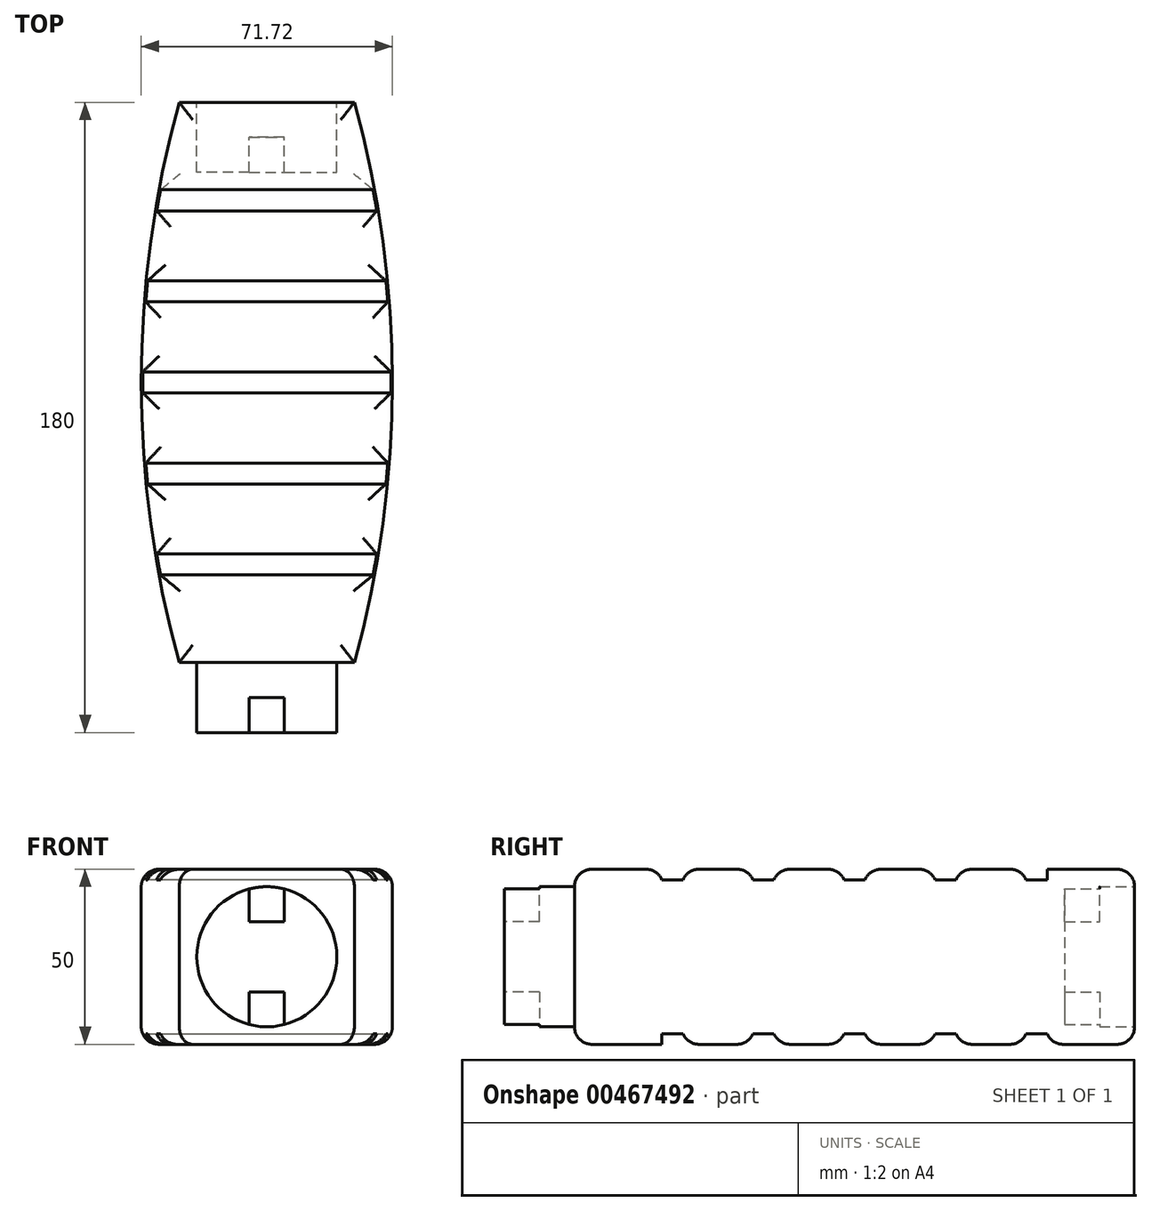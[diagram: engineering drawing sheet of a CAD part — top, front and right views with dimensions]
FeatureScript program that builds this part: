
annotation { "Feature Type Name" : "Feature", "Feature Type Description" : "" }
export const myFeature = defineFeature(function(context is Context, id is Id, definition is map)
    precondition{}
    {
        {
            var Q0;
            Q0=qCreatedBy(makeId("Top.planeOp"),FACE);
            var sketch = newSketch(context, id + "F0", { "sketchPlane" : qUnion([Q0])});
            skLineSegment(sketch, "E0.bottom", {"start": v(25, -80) * mm, "end": v(-25, -80) * mm});
            skLineSegment(sketch, "E0.top", {"start": v(25, 80) * mm, "end": v(-25, 80) * mm});
            skLineSegment(sketch, "E0.left", {"start": v(25, -80) * mm, "end": v(25, 80) * mm});
            skLineSegment(sketch, "E0.right", {"start": v(-25, -80) * mm, "end": v(-25, 80) * mm});
            skPoint(sketch, "E0.middle", {"position": v(0, 0) * mm});
            skArc(sketch, "E1", {"start": v(-25, 80) * mm, "mid": v(-35.86, 0) * mm, "end": v(-25, -80) * mm});
            skArc(sketch, "E2", {"start": v(25, -80) * mm, "mid": v(35.86, 0) * mm, "end": v(25, 80) * mm});
            skSolve(sketch);
        }
        {
            var Q0;
            Q0=makeQuery(id+"F0.imprint","IMPRINT",FACE,{"disambiguationData":[TD([[makeQuery(id+"F0.imprint","IMPRINT",EDGE,{"derivedFrom":sQuery(id+"F0.wireOp",EDGE,"E0.bottom")}),-1.0]])]});
            var Q1;
            Q1=makeQuery(id+"F0.imprint","IMPRINT",FACE,{"disambiguationData":[TD([[makeQuery(id+"F0.imprint","IMPRINT",EDGE,{"derivedFrom":sQuery(id+"F0.wireOp",EDGE,"E0.left")}),-1.0]])]});
            var Q2;
            Q2=makeQuery(id+"F0.imprint","IMPRINT",FACE,{"disambiguationData":[TD([[makeQuery(id+"F0.imprint","IMPRINT",EDGE,{"derivedFrom":sQuery(id+"F0.wireOp",EDGE,"E0.right")}),1.0]])]});
            extrude(context, id + "F1", {"entities" : qUnion([Q0, Q1, Q2]), "depth" : 50 * mm});
        }
        {
            var Q0;
            Q0=makeQuery(id+"F1.opExtrude","SWEPT_FACE",FACE,{"disambiguationData":[OSD([sQuery(id+"F0.wireOp",EDGE,"E0.bottom")])]});
            var sketch = newSketch(context, id + "F2", { "sketchPlane" : qUnion([Q0])});
            skCircle(sketch, "E3", {"center": v(0, 25) * mm, "radius": 20 * mm});
            skPoint(sketch, "E3.centerSnap0", {"position": v(25, 25) * mm});
            skSolve(sketch);
        }
        {
            var Q0;
            Q0=makeQuery(id+"F2.imprint","IMPRINT",FACE,{"disambiguationData":[TD([[makeQuery(id+"F2.imprint","IMPRINT",EDGE,{"derivedFrom":sQuery(id+"F2.wireOp",EDGE,"E3")}),1.0]])]});
            extrude(context, id + "F3", {"entities" : qUnion([Q0]), "operationType" : NewBodyOperationType.ADD, "depth" : 20 * mm});
        }
        {
            var Q0;
            Q0=makeQuery(id+"F3.opExtrude","CAP_FACE",FACE,{"disambiguationData":[OSD([sQuery(id+"F2.wireOp",EDGE,"E3")])],"isStart":false});
            var sketch = newSketch(context, id + "F4", { "sketchPlane" : qUnion([Q0])});
            skLineSegment(sketch, "E4", {"start": v(0, 45) * mm, "end": v(0, 35) * mm});
            skLineSegment(sketch, "E5", {"start": v(0, 35) * mm, "end": v(5, 35) * mm});
            skLineSegment(sketch, "E6", {"start": v(5, 35) * mm, "end": v(5, 44.36) * mm});
            skLineSegment(sketch, "E7", {"start": v(0, 35) * mm, "end": v(-5, 35) * mm});
            skLineSegment(sketch, "E8", {"start": v(-5, 35) * mm, "end": v(-5, 44.36) * mm});
            skLineSegment(sketch, "E9", {"start": v(0, 5) * mm, "end": v(0, 15) * mm});
            skLineSegment(sketch, "E10", {"start": v(0, 15) * mm, "end": v(5, 15) * mm});
            skLineSegment(sketch, "E11", {"start": v(5, 15) * mm, "end": v(5, 5.64) * mm});
            skLineSegment(sketch, "E12", {"start": v(0, 15) * mm, "end": v(-5, 15) * mm});
            skLineSegment(sketch, "E13", {"start": v(-5, 15) * mm, "end": v(-5, 5.64) * mm});
            skSolve(sketch);
        }
        {
            var Q0;
            Q0 = qSketchRegion(id + "F4", true);
            var Q1;
            {var subQ0=sQuery(id+"F4.wireOp",EDGE,"E4");Q1=makeQuery(id+"F4.imprint","IMPRINT",FACE,{"disambiguationData":[TD([[makeQuery(id+"F4.imprint","IMPRINT",EDGE,{"derivedFrom":subQ0}),1.0]])]});}
            var Q2;
            {var subQ0=sQuery(id+"F4.wireOp",EDGE,"E4");Q2=makeQuery(id+"F4.imprint","IMPRINT",FACE,{"disambiguationData":[TD([[makeQuery(id+"F4.imprint","IMPRINT",EDGE,{"derivedFrom":subQ0}),-1.0]])]});}
            var Q3;
            {var subQ0=sQuery(id+"F4.wireOp",EDGE,"E9");Q3=makeQuery(id+"F4.imprint","IMPRINT",FACE,{"disambiguationData":[TD([[makeQuery(id+"F4.imprint","IMPRINT",EDGE,{"derivedFrom":subQ0}),-1.0]])]});}
            var Q4;
            {var subQ0=sQuery(id+"F4.wireOp",EDGE,"E9");Q4=makeQuery(id+"F4.imprint","IMPRINT",FACE,{"disambiguationData":[TD([[makeQuery(id+"F4.imprint","IMPRINT",EDGE,{"derivedFrom":subQ0}),1.0]])]});}
            extrude(context, id + "F5", {"entities" : qUnion([Q0, Q1, Q2, Q3, Q4]), "operationType" : NewBodyOperationType.REMOVE, "oppositeDirection" : true, "depth" : 10 * mm});
        }
        {
            var Q0;
            Q0=makeQuery(id+"F1.opExtrude","CAP_FACE",FACE,{"disambiguationData":[OSD([sQuery(id+"F0.wireOp",EDGE,"E0.bottom"),sQuery(id+"F0.wireOp",EDGE,"E0.top"),sQuery(id+"F0.wireOp",EDGE,"E1"),sQuery(id+"F0.wireOp",EDGE,"E2")])],"isStart":false});
            var Q1;
            Q1=makeQuery(id+"F1.opExtrude","CAP_FACE",FACE,{"disambiguationData":[OSD([sQuery(id+"F0.wireOp",EDGE,"E0.bottom"),sQuery(id+"F0.wireOp",EDGE,"E0.top"),sQuery(id+"F0.wireOp",EDGE,"E1"),sQuery(id+"F0.wireOp",EDGE,"E2")])],"isStart":true});
            fillet(context, id + "F6", {"entities" : qUnion([Q0, Q1]), "radius" : 5 * mm, "tangentPropagation" : true, "allowEdgeOverflow" : false});
        }
        {
            var Q0;
            Q0=makeQuery(id+"F1.opExtrude","CAP_FACE",FACE,{"disambiguationData":[OSD([sQuery(id+"F0.wireOp",EDGE,"E0.bottom"),sQuery(id+"F0.wireOp",EDGE,"E0.top"),sQuery(id+"F0.wireOp",EDGE,"E1"),sQuery(id+"F0.wireOp",EDGE,"E2")])],"isStart":false});
            var sketch = newSketch(context, id + "F7", { "sketchPlane" : qUnion([Q0])});
            skLineSegment(sketch, "E14.bottom", {"start": v(57.86, 49) * mm, "end": v(-57.86, 49) * mm});
            skLineSegment(sketch, "E14.top", {"start": v(57.86, 55) * mm, "end": v(-57.86, 55) * mm});
            skLineSegment(sketch, "E14.left", {"start": v(57.86, 49) * mm, "end": v(57.86, 55) * mm});
            skLineSegment(sketch, "E14.right", {"start": v(-57.86, 49) * mm, "end": v(-57.86, 55) * mm});
            skPoint(sketch, "E14.middle", {"position": v(0, 52) * mm});
            skLineSegment(sketch, "E15.bottom", {"start": v(57.86, 23) * mm, "end": v(-57.86, 23) * mm});
            skLineSegment(sketch, "E15.top", {"start": v(57.86, 29) * mm, "end": v(-57.86, 29) * mm});
            skLineSegment(sketch, "E15.left", {"start": v(57.86, 23) * mm, "end": v(57.86, 29) * mm});
            skLineSegment(sketch, "E15.right", {"start": v(-57.86, 23) * mm, "end": v(-57.86, 29) * mm});
            skPoint(sketch, "E15.middle", {"position": v(0, 26) * mm});
            skLineSegment(sketch, "E16.bottom", {"start": v(59.06, -3) * mm, "end": v(-59.06, -3) * mm});
            skLineSegment(sketch, "E16.top", {"start": v(59.06, 3) * mm, "end": v(-59.06, 3) * mm});
            skLineSegment(sketch, "E16.left", {"start": v(59.06, -3) * mm, "end": v(59.06, 3) * mm});
            skLineSegment(sketch, "E16.right", {"start": v(-59.06, -3) * mm, "end": v(-59.06, 3) * mm});
            skPoint(sketch, "E16.middle", {"position": v(0, 0) * mm});
            skLineSegment(sketch, "E17.bottom", {"start": v(59.06, -29) * mm, "end": v(-59.06, -29) * mm});
            skLineSegment(sketch, "E17.top", {"start": v(59.06, -23) * mm, "end": v(-59.06, -23) * mm});
            skLineSegment(sketch, "E17.left", {"start": v(59.06, -29) * mm, "end": v(59.06, -23) * mm});
            skLineSegment(sketch, "E17.right", {"start": v(-59.06, -29) * mm, "end": v(-59.06, -23) * mm});
            skPoint(sketch, "E17.middle", {"position": v(0, -26) * mm});
            skLineSegment(sketch, "E18.bottom", {"start": v(63.4, -55) * mm, "end": v(-63.4, -55) * mm});
            skLineSegment(sketch, "E18.top", {"start": v(63.4, -49) * mm, "end": v(-63.4, -49) * mm});
            skLineSegment(sketch, "E18.left", {"start": v(63.4, -55) * mm, "end": v(63.4, -49) * mm});
            skLineSegment(sketch, "E18.right", {"start": v(-63.4, -55) * mm, "end": v(-63.4, -49) * mm});
            skPoint(sketch, "E18.middle", {"position": v(0, -52) * mm});
            skSolve(sketch);
        }
        {
            var Q0;
            {var subQ0=sQuery(id+"F7.wireOp",EDGE,"E14.right");Q0=makeQuery(id+"F7.imprint","IMPRINT",FACE,{"disambiguationData":[TD([[makeQuery(id+"F7.imprint","IMPRINT",EDGE,{"derivedFrom":subQ0}),-1.0]])]});}
            var Q1;
            {var subQ0=sQuery(id+"F7.wireOp",EDGE,"E14.left");Q1=makeQuery(id+"F7.imprint","IMPRINT",FACE,{"disambiguationData":[TD([[makeQuery(id+"F7.imprint","IMPRINT",EDGE,{"derivedFrom":subQ0}),1.0]])]});}
            var Q2;
            {var subQ0=sQuery(id+"F7.wireOp",EDGE,"E14.bottom");var subQ1=sQuery(id+"F0.wireOp",EDGE,"E2");var subQ2=sQuery(id+"F0.wireOp",EDGE,"E1");var subQ3=makeQuery(id+"F1.opExtrude","CAP_FACE",FACE,{"disambiguationData":[OSD([sQuery(id+"F0.wireOp",EDGE,"E0.bottom"),sQuery(id+"F0.wireOp",EDGE,"E0.top"),subQ2,subQ1])],"isStart":false});var subQ4=makeQuery(id+"F6.opFillet","BLEND_EDGE",EDGE,{"blendedFrom":[makeQuery(id+"F1.opExtrude","CAP_EDGE",EDGE,{"disambiguationData":[OSD([subQ1])],"isStart":false}),subQ3],"blendedInto":[subQ3]});var subQ5=makeQuery(id+"F7.imprint","INTERSECT",VERTEX,{"derivedFrom":[subQ4,subQ0]});Q2=makeQuery(id+"F7.imprint","IMPRINT",FACE,{"disambiguationData":[TD([[makeQuery(id+"F7.imprint","IMPRINT",EDGE,{"disambiguationData":[TD([[subQ5,-1.0]])],"derivedFrom":subQ0}),-1.0]])]});}
            var Q3;
            {var subQ0=sQuery(id+"F7.wireOp",EDGE,"E15.left");Q3=makeQuery(id+"F7.imprint","IMPRINT",FACE,{"disambiguationData":[TD([[makeQuery(id+"F7.imprint","IMPRINT",EDGE,{"derivedFrom":subQ0}),1.0]])]});}
            var Q4;
            {var subQ0=sQuery(id+"F7.wireOp",EDGE,"E15.bottom");var subQ1=sQuery(id+"F0.wireOp",EDGE,"E2");var subQ2=sQuery(id+"F0.wireOp",EDGE,"E1");var subQ3=makeQuery(id+"F1.opExtrude","CAP_FACE",FACE,{"disambiguationData":[OSD([sQuery(id+"F0.wireOp",EDGE,"E0.bottom"),sQuery(id+"F0.wireOp",EDGE,"E0.top"),subQ2,subQ1])],"isStart":false});var subQ4=makeQuery(id+"F6.opFillet","BLEND_EDGE",EDGE,{"blendedFrom":[makeQuery(id+"F1.opExtrude","CAP_EDGE",EDGE,{"disambiguationData":[OSD([subQ1])],"isStart":false}),subQ3],"blendedInto":[subQ3]});var subQ5=makeQuery(id+"F7.imprint","INTERSECT",VERTEX,{"derivedFrom":[subQ4,subQ0]});Q4=makeQuery(id+"F7.imprint","IMPRINT",FACE,{"disambiguationData":[TD([[makeQuery(id+"F7.imprint","IMPRINT",EDGE,{"disambiguationData":[TD([[subQ5,-1.0]])],"derivedFrom":subQ0}),-1.0]])]});}
            var Q5;
            {var subQ0=sQuery(id+"F7.wireOp",EDGE,"E15.right");Q5=makeQuery(id+"F7.imprint","IMPRINT",FACE,{"disambiguationData":[TD([[makeQuery(id+"F7.imprint","IMPRINT",EDGE,{"derivedFrom":subQ0}),-1.0]])]});}
            var Q6;
            {var subQ0=sQuery(id+"F7.wireOp",EDGE,"E16.left");Q6=makeQuery(id+"F7.imprint","IMPRINT",FACE,{"disambiguationData":[TD([[makeQuery(id+"F7.imprint","IMPRINT",EDGE,{"derivedFrom":subQ0}),1.0]])]});}
            var Q7;
            {var subQ0=sQuery(id+"F7.wireOp",EDGE,"E16.bottom");var subQ1=sQuery(id+"F0.wireOp",EDGE,"E2");var subQ2=sQuery(id+"F0.wireOp",EDGE,"E1");var subQ3=makeQuery(id+"F1.opExtrude","CAP_FACE",FACE,{"disambiguationData":[OSD([sQuery(id+"F0.wireOp",EDGE,"E0.bottom"),sQuery(id+"F0.wireOp",EDGE,"E0.top"),subQ2,subQ1])],"isStart":false});var subQ4=makeQuery(id+"F6.opFillet","BLEND_EDGE",EDGE,{"blendedFrom":[makeQuery(id+"F1.opExtrude","CAP_EDGE",EDGE,{"disambiguationData":[OSD([subQ1])],"isStart":false}),subQ3],"blendedInto":[subQ3]});var subQ5=makeQuery(id+"F7.imprint","INTERSECT",VERTEX,{"derivedFrom":[subQ4,subQ0]});Q7=makeQuery(id+"F7.imprint","IMPRINT",FACE,{"disambiguationData":[TD([[makeQuery(id+"F7.imprint","IMPRINT",EDGE,{"disambiguationData":[TD([[subQ5,-1.0]])],"derivedFrom":subQ0}),-1.0]])]});}
            var Q8;
            {var subQ0=sQuery(id+"F7.wireOp",EDGE,"E16.right");Q8=makeQuery(id+"F7.imprint","IMPRINT",FACE,{"disambiguationData":[TD([[makeQuery(id+"F7.imprint","IMPRINT",EDGE,{"derivedFrom":subQ0}),-1.0]])]});}
            var Q9;
            {var subQ0=sQuery(id+"F7.wireOp",EDGE,"E17.left");Q9=makeQuery(id+"F7.imprint","IMPRINT",FACE,{"disambiguationData":[TD([[makeQuery(id+"F7.imprint","IMPRINT",EDGE,{"derivedFrom":subQ0}),1.0]])]});}
            var Q10;
            {var subQ0=sQuery(id+"F7.wireOp",EDGE,"E17.bottom");var subQ1=sQuery(id+"F0.wireOp",EDGE,"E2");var subQ2=sQuery(id+"F0.wireOp",EDGE,"E1");var subQ3=makeQuery(id+"F1.opExtrude","CAP_FACE",FACE,{"disambiguationData":[OSD([sQuery(id+"F0.wireOp",EDGE,"E0.bottom"),sQuery(id+"F0.wireOp",EDGE,"E0.top"),subQ2,subQ1])],"isStart":false});var subQ4=makeQuery(id+"F6.opFillet","BLEND_EDGE",EDGE,{"blendedFrom":[makeQuery(id+"F1.opExtrude","CAP_EDGE",EDGE,{"disambiguationData":[OSD([subQ1])],"isStart":false}),subQ3],"blendedInto":[subQ3]});var subQ5=makeQuery(id+"F7.imprint","INTERSECT",VERTEX,{"derivedFrom":[subQ4,subQ0]});Q10=makeQuery(id+"F7.imprint","IMPRINT",FACE,{"disambiguationData":[TD([[makeQuery(id+"F7.imprint","IMPRINT",EDGE,{"disambiguationData":[TD([[subQ5,-1.0]])],"derivedFrom":subQ0}),-1.0]])]});}
            var Q11;
            {var subQ0=sQuery(id+"F7.wireOp",EDGE,"E17.right");Q11=makeQuery(id+"F7.imprint","IMPRINT",FACE,{"disambiguationData":[TD([[makeQuery(id+"F7.imprint","IMPRINT",EDGE,{"derivedFrom":subQ0}),-1.0]])]});}
            var Q12;
            {var subQ0=sQuery(id+"F7.wireOp",EDGE,"E18.right");Q12=makeQuery(id+"F7.imprint","IMPRINT",FACE,{"disambiguationData":[TD([[makeQuery(id+"F7.imprint","IMPRINT",EDGE,{"derivedFrom":subQ0}),-1.0]])]});}
            var Q13;
            {var subQ0=sQuery(id+"F7.wireOp",EDGE,"E18.bottom");var subQ1=sQuery(id+"F0.wireOp",EDGE,"E2");var subQ2=sQuery(id+"F0.wireOp",EDGE,"E1");var subQ3=makeQuery(id+"F1.opExtrude","CAP_FACE",FACE,{"disambiguationData":[OSD([sQuery(id+"F0.wireOp",EDGE,"E0.bottom"),sQuery(id+"F0.wireOp",EDGE,"E0.top"),subQ2,subQ1])],"isStart":false});var subQ4=makeQuery(id+"F6.opFillet","BLEND_EDGE",EDGE,{"blendedFrom":[makeQuery(id+"F1.opExtrude","CAP_EDGE",EDGE,{"disambiguationData":[OSD([subQ1])],"isStart":false}),subQ3],"blendedInto":[subQ3]});var subQ5=makeQuery(id+"F7.imprint","INTERSECT",VERTEX,{"derivedFrom":[subQ4,subQ0]});Q13=makeQuery(id+"F7.imprint","IMPRINT",FACE,{"disambiguationData":[TD([[makeQuery(id+"F7.imprint","IMPRINT",EDGE,{"disambiguationData":[TD([[subQ5,-1.0]])],"derivedFrom":subQ0}),-1.0]])]});}
            var Q14;
            {var subQ0=sQuery(id+"F7.wireOp",EDGE,"E18.left");Q14=makeQuery(id+"F7.imprint","IMPRINT",FACE,{"disambiguationData":[TD([[makeQuery(id+"F7.imprint","IMPRINT",EDGE,{"derivedFrom":subQ0}),1.0]])]});}
            extrude(context, id + "F8", {"entities" : qUnion([Q0, Q1, Q2, Q3, Q4, Q5, Q6, Q7, Q8, Q9, Q10, Q11, Q12, Q13, Q14]), "operationType" : NewBodyOperationType.REMOVE, "oppositeDirection" : true, "depth" : 3 * mm});
        }
        {
            var Q0;
            Q0=makeQuery(id+"F8.boolean.opBoolean","COPY",EDGE,{"derivedFrom":makeQuery(id+"F8.opExtrude","CAP_EDGE",EDGE,{"disambiguationData":[OSD([sQuery(id+"F7.wireOp",EDGE,"E14.top")])],"isStart":true})});
            var Q1;
            Q1=makeQuery(id+"F8.boolean.opBoolean","COPY",EDGE,{"derivedFrom":makeQuery(id+"F8.opExtrude","CAP_EDGE",EDGE,{"disambiguationData":[OSD([sQuery(id+"F7.wireOp",EDGE,"E14.bottom")])],"isStart":true})});
            var Q2;
            Q2=makeQuery(id+"F8.boolean.opBoolean","COPY",EDGE,{"derivedFrom":makeQuery(id+"F8.opExtrude","CAP_EDGE",EDGE,{"disambiguationData":[OSD([sQuery(id+"F7.wireOp",EDGE,"E15.top")])],"isStart":true})});
            var Q3;
            Q3=makeQuery(id+"F8.boolean.opBoolean","COPY",EDGE,{"derivedFrom":makeQuery(id+"F8.opExtrude","CAP_EDGE",EDGE,{"disambiguationData":[OSD([sQuery(id+"F7.wireOp",EDGE,"E15.bottom")])],"isStart":true})});
            var Q4;
            Q4=makeQuery(id+"F8.boolean.opBoolean","COPY",EDGE,{"derivedFrom":makeQuery(id+"F8.opExtrude","CAP_EDGE",EDGE,{"disambiguationData":[OSD([sQuery(id+"F7.wireOp",EDGE,"E16.top")])],"isStart":true})});
            var Q5;
            Q5=makeQuery(id+"F8.boolean.opBoolean","COPY",EDGE,{"derivedFrom":makeQuery(id+"F8.opExtrude","CAP_EDGE",EDGE,{"disambiguationData":[OSD([sQuery(id+"F7.wireOp",EDGE,"E16.bottom")])],"isStart":true})});
            var Q6;
            Q6=makeQuery(id+"F8.boolean.opBoolean","COPY",EDGE,{"derivedFrom":makeQuery(id+"F8.opExtrude","CAP_EDGE",EDGE,{"disambiguationData":[OSD([sQuery(id+"F7.wireOp",EDGE,"E17.top")])],"isStart":true})});
            var Q7;
            Q7=makeQuery(id+"F8.boolean.opBoolean","COPY",EDGE,{"derivedFrom":makeQuery(id+"F8.opExtrude","CAP_EDGE",EDGE,{"disambiguationData":[OSD([sQuery(id+"F7.wireOp",EDGE,"E17.bottom")])],"isStart":true})});
            var Q8;
            Q8=makeQuery(id+"F8.boolean.opBoolean","COPY",EDGE,{"derivedFrom":makeQuery(id+"F8.opExtrude","CAP_EDGE",EDGE,{"disambiguationData":[OSD([sQuery(id+"F7.wireOp",EDGE,"E18.top")])],"isStart":true})});
            var Q9;
            Q9=makeQuery(id+"F8.boolean.opBoolean","COPY",EDGE,{"derivedFrom":makeQuery(id+"F8.opExtrude","CAP_EDGE",EDGE,{"disambiguationData":[OSD([sQuery(id+"F7.wireOp",EDGE,"E18.bottom")])],"isStart":true})});
            fillet(context, id + "F9", {"entities" : qUnion([Q0, Q1, Q2, Q3, Q4, Q5, Q6, Q7, Q8, Q9]), "radius" : 5 * mm, "tangentPropagation" : true, "allowEdgeOverflow" : false});
        }
        {
            var Q0;
            Q0=makeQuery(id+"F1.opExtrude","CAP_FACE",FACE,{"disambiguationData":[OSD([sQuery(id+"F0.wireOp",EDGE,"E0.bottom"),sQuery(id+"F0.wireOp",EDGE,"E0.top"),sQuery(id+"F0.wireOp",EDGE,"E1"),sQuery(id+"F0.wireOp",EDGE,"E2")])],"isStart":true});
            var sketch = newSketch(context, id + "F10", { "sketchPlane" : qUnion([Q0])});
            skLineSegment(sketch, "E19.bottom", {"start": v(-45.48, -55) * mm, "end": v(45.48, -55) * mm});
            skLineSegment(sketch, "E19.top", {"start": v(-45.48, -49) * mm, "end": v(45.48, -49) * mm});
            skLineSegment(sketch, "E19.left", {"start": v(-45.48, -55) * mm, "end": v(-45.48, -49) * mm});
            skLineSegment(sketch, "E19.right", {"start": v(45.48, -55) * mm, "end": v(45.48, -49) * mm});
            skPoint(sketch, "E19.middle", {"position": v(0, -52) * mm});
            skLineSegment(sketch, "E20.bottom", {"start": v(-38.25, -29) * mm, "end": v(38.25, -29) * mm});
            skLineSegment(sketch, "E20.top", {"start": v(-38.25, -23) * mm, "end": v(38.25, -23) * mm});
            skLineSegment(sketch, "E20.left", {"start": v(-38.25, -29) * mm, "end": v(-38.25, -23) * mm});
            skLineSegment(sketch, "E20.right", {"start": v(38.25, -29) * mm, "end": v(38.25, -23) * mm});
            skPoint(sketch, "E20.middle", {"position": v(0, -26) * mm});
            skLineSegment(sketch, "E21.bottom", {"start": v(-45.48, 3) * mm, "end": v(45.48, 3) * mm});
            skLineSegment(sketch, "E21.top", {"start": v(-45.48, -3) * mm, "end": v(45.48, -3) * mm});
            skLineSegment(sketch, "E21.left", {"start": v(-45.48, 3) * mm, "end": v(-45.48, -3) * mm});
            skLineSegment(sketch, "E21.right", {"start": v(45.48, 3) * mm, "end": v(45.48, -3) * mm});
            skPoint(sketch, "E21.middle", {"position": v(0, 0) * mm});
            skLineSegment(sketch, "E22.bottom", {"start": v(-45.48, 29) * mm, "end": v(45.48, 29) * mm});
            skLineSegment(sketch, "E22.top", {"start": v(-45.48, 23) * mm, "end": v(45.48, 23) * mm});
            skLineSegment(sketch, "E22.left", {"start": v(-45.48, 29) * mm, "end": v(-45.48, 23) * mm});
            skLineSegment(sketch, "E22.right", {"start": v(45.48, 29) * mm, "end": v(45.48, 23) * mm});
            skPoint(sketch, "E22.middle", {"position": v(0, 26) * mm});
            skLineSegment(sketch, "E23.bottom", {"start": v(-38.25, 49) * mm, "end": v(38.25, 49) * mm});
            skLineSegment(sketch, "E23.top", {"start": v(-38.25, 55) * mm, "end": v(38.25, 55) * mm});
            skLineSegment(sketch, "E23.left", {"start": v(-38.25, 49) * mm, "end": v(-38.25, 55) * mm});
            skLineSegment(sketch, "E23.right", {"start": v(38.25, 49) * mm, "end": v(38.25, 55) * mm});
            skPoint(sketch, "E23.middle", {"position": v(0, 52) * mm});
            skSolve(sketch);
        }
        {
            var Q0;
            Q0 = qSketchRegion(id + "F10", true);
            extrude(context, id + "F11", {"entities" : qUnion([Q0]), "operationType" : NewBodyOperationType.REMOVE, "oppositeDirection" : true, "depth" : 3 * mm});
        }
        {
            var Q0;
            Q0=makeQuery(id+"F11.boolean.opBoolean","COPY",EDGE,{"derivedFrom":makeQuery(id+"F11.opExtrude","CAP_EDGE",EDGE,{"disambiguationData":[OSD([sQuery(id+"F10.wireOp",EDGE,"E19.bottom")])],"isStart":true})});
            var Q1;
            Q1=makeQuery(id+"F11.boolean.opBoolean","COPY",EDGE,{"derivedFrom":makeQuery(id+"F11.opExtrude","CAP_EDGE",EDGE,{"disambiguationData":[OSD([sQuery(id+"F10.wireOp",EDGE,"E19.top")])],"isStart":true})});
            var Q2;
            Q2=makeQuery(id+"F11.boolean.opBoolean","COPY",EDGE,{"derivedFrom":makeQuery(id+"F11.opExtrude","CAP_EDGE",EDGE,{"disambiguationData":[OSD([sQuery(id+"F10.wireOp",EDGE,"E20.bottom")])],"isStart":true})});
            var Q3;
            Q3=makeQuery(id+"F11.boolean.opBoolean","COPY",EDGE,{"derivedFrom":makeQuery(id+"F11.opExtrude","CAP_EDGE",EDGE,{"disambiguationData":[OSD([sQuery(id+"F10.wireOp",EDGE,"E20.top")])],"isStart":true})});
            var Q4;
            Q4=makeQuery(id+"F11.boolean.opBoolean","COPY",EDGE,{"derivedFrom":makeQuery(id+"F11.opExtrude","CAP_EDGE",EDGE,{"disambiguationData":[OSD([sQuery(id+"F10.wireOp",EDGE,"E21.top")])],"isStart":true})});
            var Q5;
            Q5=makeQuery(id+"F11.boolean.opBoolean","COPY",EDGE,{"derivedFrom":makeQuery(id+"F11.opExtrude","CAP_EDGE",EDGE,{"disambiguationData":[OSD([sQuery(id+"F10.wireOp",EDGE,"E21.bottom")])],"isStart":true})});
            var Q6;
            Q6=makeQuery(id+"F11.boolean.opBoolean","COPY",EDGE,{"derivedFrom":makeQuery(id+"F11.opExtrude","CAP_EDGE",EDGE,{"disambiguationData":[OSD([sQuery(id+"F10.wireOp",EDGE,"E22.top")])],"isStart":true})});
            var Q7;
            Q7=makeQuery(id+"F11.boolean.opBoolean","COPY",EDGE,{"derivedFrom":makeQuery(id+"F11.opExtrude","CAP_EDGE",EDGE,{"disambiguationData":[OSD([sQuery(id+"F10.wireOp",EDGE,"E22.bottom")])],"isStart":true})});
            var Q8;
            Q8=makeQuery(id+"F11.boolean.opBoolean","COPY",EDGE,{"derivedFrom":makeQuery(id+"F11.opExtrude","CAP_EDGE",EDGE,{"disambiguationData":[OSD([sQuery(id+"F10.wireOp",EDGE,"E23.bottom")])],"isStart":true})});
            var Q9;
            Q9=makeQuery(id+"F11.boolean.opBoolean","COPY",EDGE,{"derivedFrom":makeQuery(id+"F11.opExtrude","CAP_EDGE",EDGE,{"disambiguationData":[OSD([sQuery(id+"F10.wireOp",EDGE,"E23.top")])],"isStart":true})});
            fillet(context, id + "F12", {"entities" : qUnion([Q0, Q1, Q2, Q3, Q4, Q5, Q6, Q7, Q8, Q9]), "radius" : 5 * mm, "tangentPropagation" : true, "allowEdgeOverflow" : false});
        }
        {
            var Q0;
            Q0=makeQuery(id+"F1.opExtrude","SWEPT_FACE",FACE,{"disambiguationData":[OSD([sQuery(id+"F0.wireOp",EDGE,"E0.top")])]});
            var sketch = newSketch(context, id + "F13", { "sketchPlane" : qUnion([Q0])});
            skCircle(sketch, "E24", {"center": v(0, 25) * mm, "radius": 20 * mm});
            skPoint(sketch, "E24.centerSnap0", {"position": v(-25, 25) * mm});
            skLineSegment(sketch, "E25", {"start": v(0, 5) * mm, "end": v(0, 15) * mm});
            skPoint(sketch, "E25.endSnap0", {"position": v(0, 5) * mm});
            skLineSegment(sketch, "E26", {"start": v(0, 15) * mm, "end": v(-5, 15) * mm});
            skLineSegment(sketch, "E27", {"start": v(-5, 15) * mm, "end": v(-5, 5.64) * mm});
            skLineSegment(sketch, "E28", {"start": v(0, 15) * mm, "end": v(5, 15) * mm});
            skLineSegment(sketch, "E29", {"start": v(5, 15) * mm, "end": v(5, 5.64) * mm});
            skLineSegment(sketch, "E30", {"start": v(0, 45) * mm, "end": v(0, 35) * mm});
            skPoint(sketch, "E30.endSnap0", {"position": v(0, 45) * mm});
            skLineSegment(sketch, "E31", {"start": v(0, 35) * mm, "end": v(-5, 35) * mm});
            skLineSegment(sketch, "E32", {"start": v(-5, 35) * mm, "end": v(-5, 44.36) * mm});
            skLineSegment(sketch, "E33", {"start": v(0, 35) * mm, "end": v(5, 35) * mm});
            skLineSegment(sketch, "E34", {"start": v(5, 35) * mm, "end": v(5, 44.36) * mm});
            skArc(sketch, "E35", {"start": v(5, 44.36) * mm, "mid": v(0, 45) * mm, "end": v(-5, 44.36) * mm});
            skArc(sketch, "E36", {"start": v(-5, 5.64) * mm, "mid": v(0, 5) * mm, "end": v(5, 5.64) * mm});
            skSolve(sketch);
        }
        {
            var Q0;
            Q0=makeQuery(id+"F13.imprint","IMPRINT",FACE,{"disambiguationData":[TD([[makeQuery(id+"F13.imprint","IMPRINT",EDGE,{"derivedFrom":sQuery(id+"F13.wireOp",EDGE,"E26")}),-1.0]])]});
            extrude(context, id + "F14", {"entities" : qUnion([Q0]), "operationType" : NewBodyOperationType.REMOVE, "oppositeDirection" : true, "depth" : 20 * mm});
        }
        {
            var Q0;
            {var subQ0=sQuery(id+"F13.wireOp",EDGE,"E30");Q0=makeQuery(id+"F13.imprint","IMPRINT",FACE,{"disambiguationData":[TD([[makeQuery(id+"F13.imprint","IMPRINT",EDGE,{"derivedFrom":subQ0}),-1.0]])]});}
            var Q1;
            {var subQ0=sQuery(id+"F13.wireOp",EDGE,"E30");Q1=makeQuery(id+"F13.imprint","IMPRINT",FACE,{"disambiguationData":[TD([[makeQuery(id+"F13.imprint","IMPRINT",EDGE,{"derivedFrom":subQ0}),1.0]])]});}
            var Q2;
            {var subQ0=sQuery(id+"F13.wireOp",EDGE,"E25");Q2=makeQuery(id+"F13.imprint","IMPRINT",FACE,{"disambiguationData":[TD([[makeQuery(id+"F13.imprint","IMPRINT",EDGE,{"derivedFrom":subQ0}),-1.0]])]});}
            var Q3;
            {var subQ0=sQuery(id+"F13.wireOp",EDGE,"E25");Q3=makeQuery(id+"F13.imprint","IMPRINT",FACE,{"disambiguationData":[TD([[makeQuery(id+"F13.imprint","IMPRINT",EDGE,{"derivedFrom":subQ0}),1.0]])]});}
            extrude(context, id + "F15", {"entities" : qUnion([Q0, Q1, Q2, Q3]), "operationType" : NewBodyOperationType.REMOVE, "oppositeDirection" : true, "depth" : 10 * mm});
        }
    });
